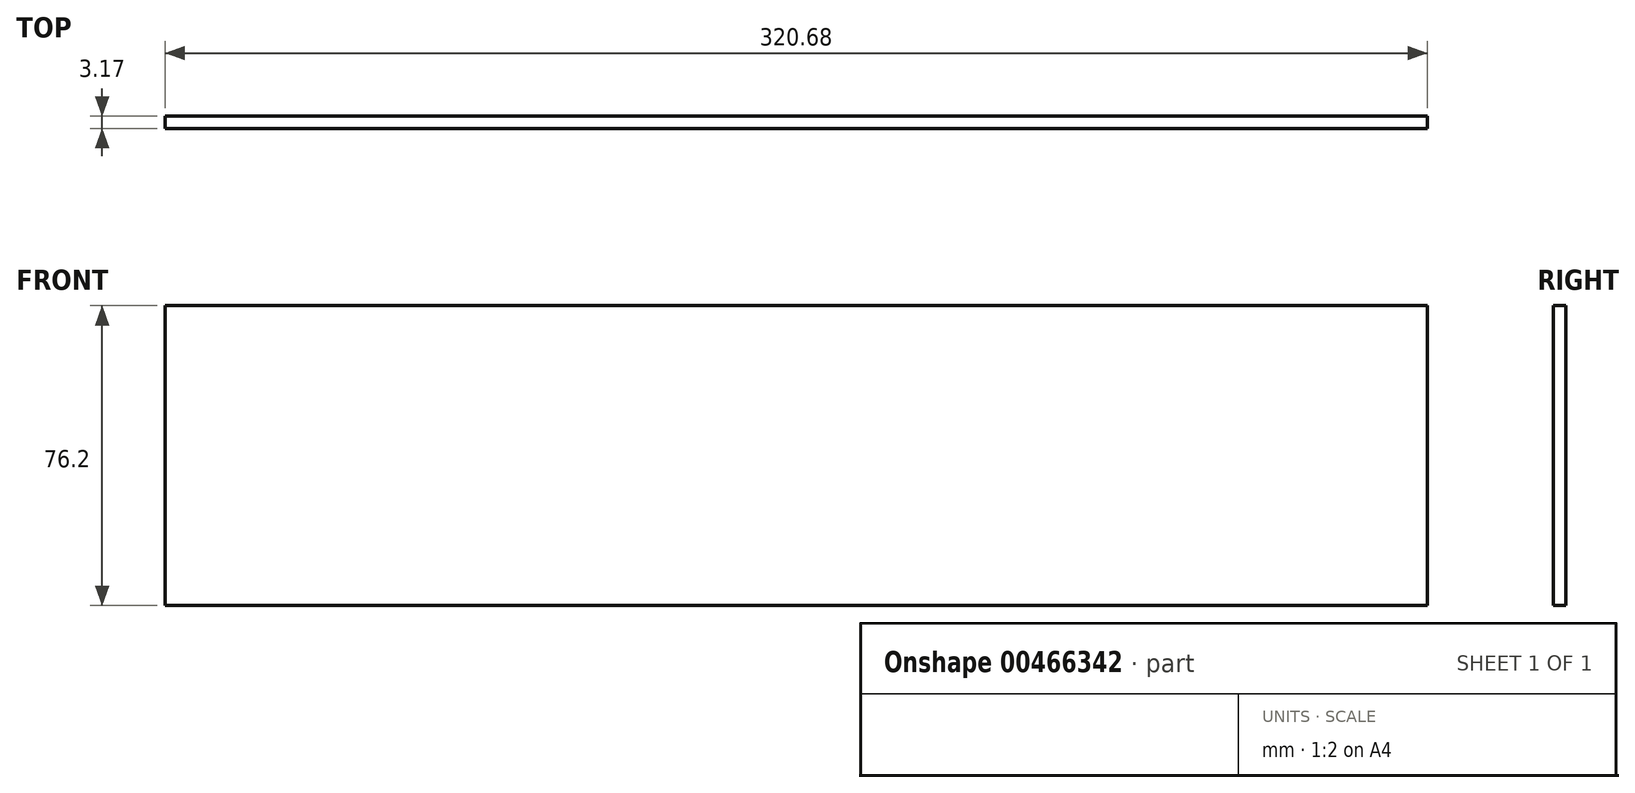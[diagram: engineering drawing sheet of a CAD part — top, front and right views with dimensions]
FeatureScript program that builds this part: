
annotation { "Feature Type Name" : "Feature", "Feature Type Description" : "" }
export const myFeature = defineFeature(function(context is Context, id is Id, definition is map)
    precondition{}
    {
        {
            var Q0;
            Q0=qCreatedBy(makeId("Front.planeOp"),FACE);
            var sketch = newSketch(context, id + "F0", { "sketchPlane" : qUnion([Q0])});
            skLineSegment(sketch, "E0.bottom", {"start": v(-159.8, 36.34) * mm, "end": v(160.87, 36.34) * mm});
            skLineSegment(sketch, "E0.top", {"start": v(-159.8, -39.86) * mm, "end": v(160.87, -39.86) * mm});
            skLineSegment(sketch, "E0.left", {"start": v(-159.8, 36.34) * mm, "end": v(-159.8, -39.86) * mm});
            skLineSegment(sketch, "E0.right", {"start": v(160.87, 36.34) * mm, "end": v(160.87, -39.86) * mm});
            skSolve(sketch);
        }
        {
            var Q0;
            Q0=makeQuery(id+"F0.imprint","IMPRINT",FACE,{"disambiguationData":[TD([[makeQuery(id+"F0.imprint","IMPRINT",EDGE,{"derivedFrom":sQuery(id+"F0.wireOp",EDGE,"E0.bottom")}),-1.0]])]});
            extrude(context, id + "F1", {"entities" : qUnion([Q0]), "depth" : 3.17 * mm});
        }
    });
